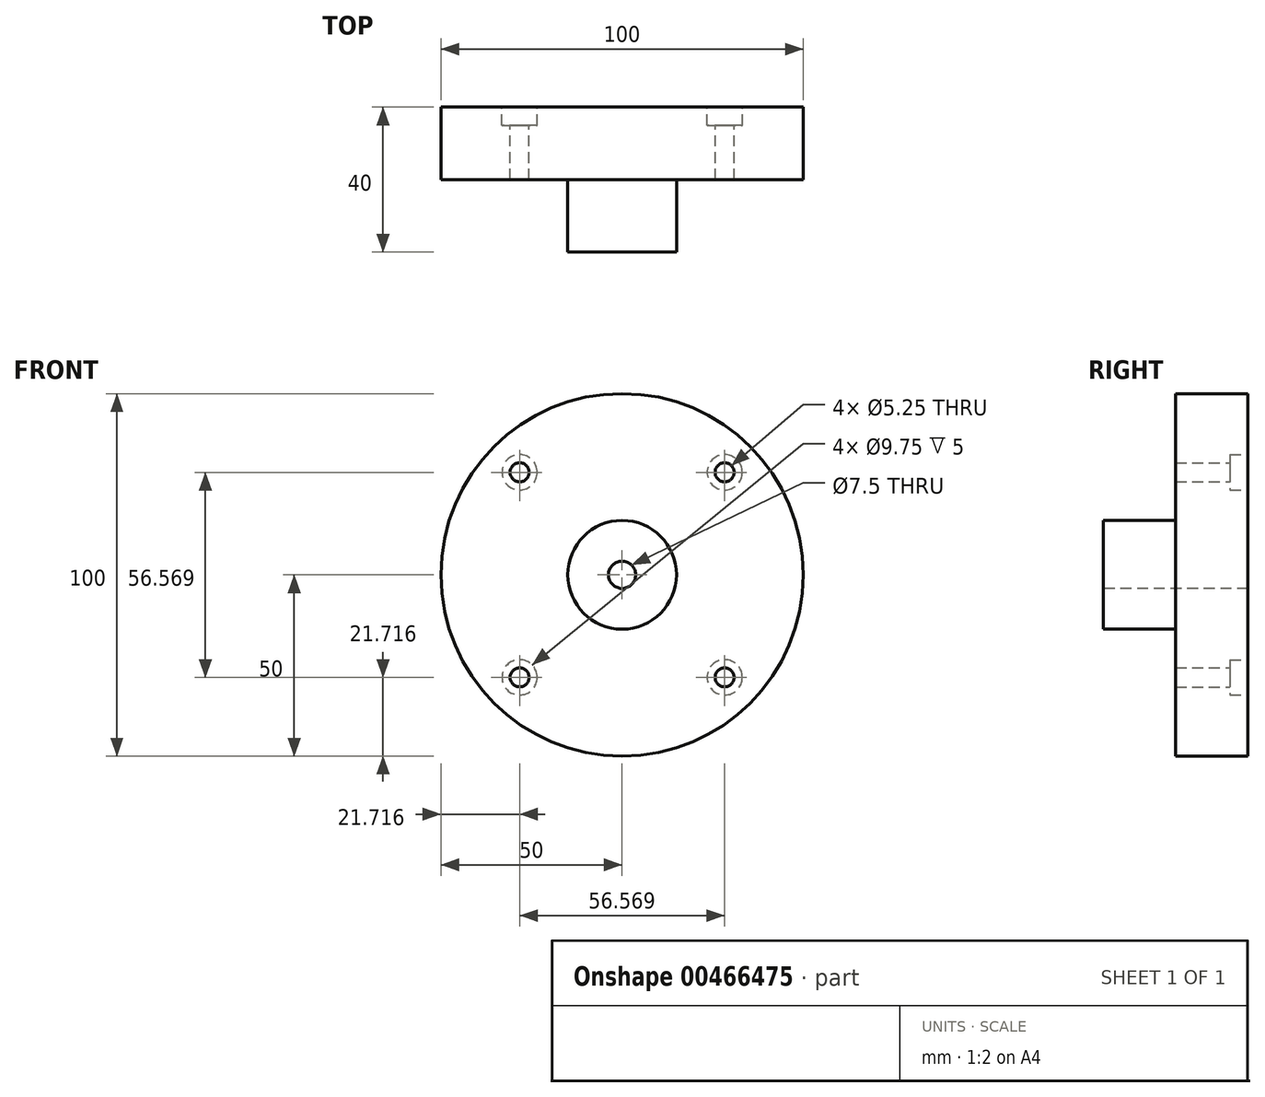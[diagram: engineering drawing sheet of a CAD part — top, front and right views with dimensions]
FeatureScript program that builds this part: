
annotation { "Feature Type Name" : "Feature", "Feature Type Description" : "" }
export const myFeature = defineFeature(function(context is Context, id is Id, definition is map)
    precondition{}
    {
        {
            var Q0;
            Q0=qCreatedBy(makeId("Top.planeOp"),FACE);
            var sketch = newSketch(context, id + "F0", { "sketchPlane" : qUnion([Q0])});
            skLineSegment(sketch, "E0", {"start": v(0, 0) * mm, "end": v(0, 40) * mm, "construction": true});
            skLineSegment(sketch, "E1", {"start": v(0, 40) * mm, "end": v(3.75, 40) * mm, "construction": true});
            skLineSegment(sketch, "E2", {"start": v(50, 40) * mm, "end": v(50, 20) * mm});
            skLineSegment(sketch, "E3", {"start": v(50, 20) * mm, "end": v(15, 20) * mm});
            skLineSegment(sketch, "E4", {"start": v(15, 20) * mm, "end": v(15, 0) * mm});
            skLineSegment(sketch, "E5", {"start": v(15, 0) * mm, "end": v(3.75, 0) * mm});
            skLineSegment(sketch, "E6", {"start": v(3.75, 40) * mm, "end": v(50, 40) * mm});
            skLineSegment(sketch, "E7", {"start": v(3.75, 0) * mm, "end": v(0, 0) * mm, "construction": true});
            skLineSegment(sketch, "E8", {"start": v(3.75, 40) * mm, "end": v(3.75, 0) * mm});
            skSolve(sketch);
        }
        {
            var Q0;
            Q0 = qSketchRegion(id + "F0", true);
            var Q1;
            Q1=sQuery(id+"F0.wireOp",EDGE,"E0");
            revolve(context, id + "F1", {"entities" : qUnion([Q0]), "axis" : qUnion([Q1]), "revolveType" : RevolveType.FULL});
        }
        {
            var Q0;
            Q0=makeQuery(id+"F1.opRevolve","SWEPT_FACE",FACE,{"disambiguationData":[OSD([sQuery(id+"F0.wireOp",EDGE,"E6")])]});
            var sketch = newSketch(context, id + "F2", { "sketchPlane" : qUnion([Q0])});
            skPoint(sketch, "E9", {"position": v(-28.28, -28.28) * mm});
            skLineSegment(sketch, "E10", {"start": v(0, 0) * mm, "end": v(-28.28, -28.28) * mm, "construction": true});
            skCircle(sketch, "E11", {"center": v(0, 0) * mm, "radius": 40 * mm, "construction": true});
            skPoint(sketch, "E12.1.0", {"position": v(28.28, -28.28) * mm});
            skPoint(sketch, "E12.2.0", {"position": v(28.28, 28.28) * mm});
            skPoint(sketch, "E12.3.0", {"position": v(-28.28, 28.28) * mm});
            skSolve(sketch);
        }
        {
            var Q0;
            Q0=sQuery(id+"F2.wireOp",VERTEX,"E12.3.0");
            var Q1;
            Q1=sQuery(id+"F2.wireOp",VERTEX,"E12.2.0");
            var Q2;
            Q2=sQuery(id+"F2.wireOp",VERTEX,"E9");
            var Q3;
            Q3=sQuery(id+"F2.wireOp",VERTEX,"E12.1.0");
            var Q4;
            Q4=makeQuery(id+"F1.opRevolve","SWEPT_BODY",BODY,{"disambiguationData":[OSD([sQuery(id+"F0.wireOp",EDGE,"E2"),sQuery(id+"F0.wireOp",EDGE,"E3"),sQuery(id+"F0.wireOp",EDGE,"E4"),sQuery(id+"F0.wireOp",EDGE,"E5"),sQuery(id+"F0.wireOp",EDGE,"E6"),sQuery(id+"F0.wireOp",EDGE,"E8")])]});
            hole(context, id + "F3", {"style" : HoleStyle.C_BORE, "endStyle" : HoleEndStyle.THROUGH, "standardTappedOrClearance" : lookupTablePath({ "standard" : "ISO", "fit" : "Close", "size" : "M5", "type" : "Clearance" }), "standardBlindInLast" : lookupTablePath({ "fit" : "Close", "standard" : "ISO", "size" : "M5", "type" : "Clearance" }), "holeDiameter" : 5.25 * mm, "cBoreDiameter" : 9.75 * mm, "cBoreDepth" : 5 * mm, "isTappedThrough" : true, "tappedDepth" : 12 * mm, "tapClearance" : 3, "locations" : qUnion([Q0, Q1, Q2, Q3]), "scope" : qUnion([Q4])});
        }
    });
